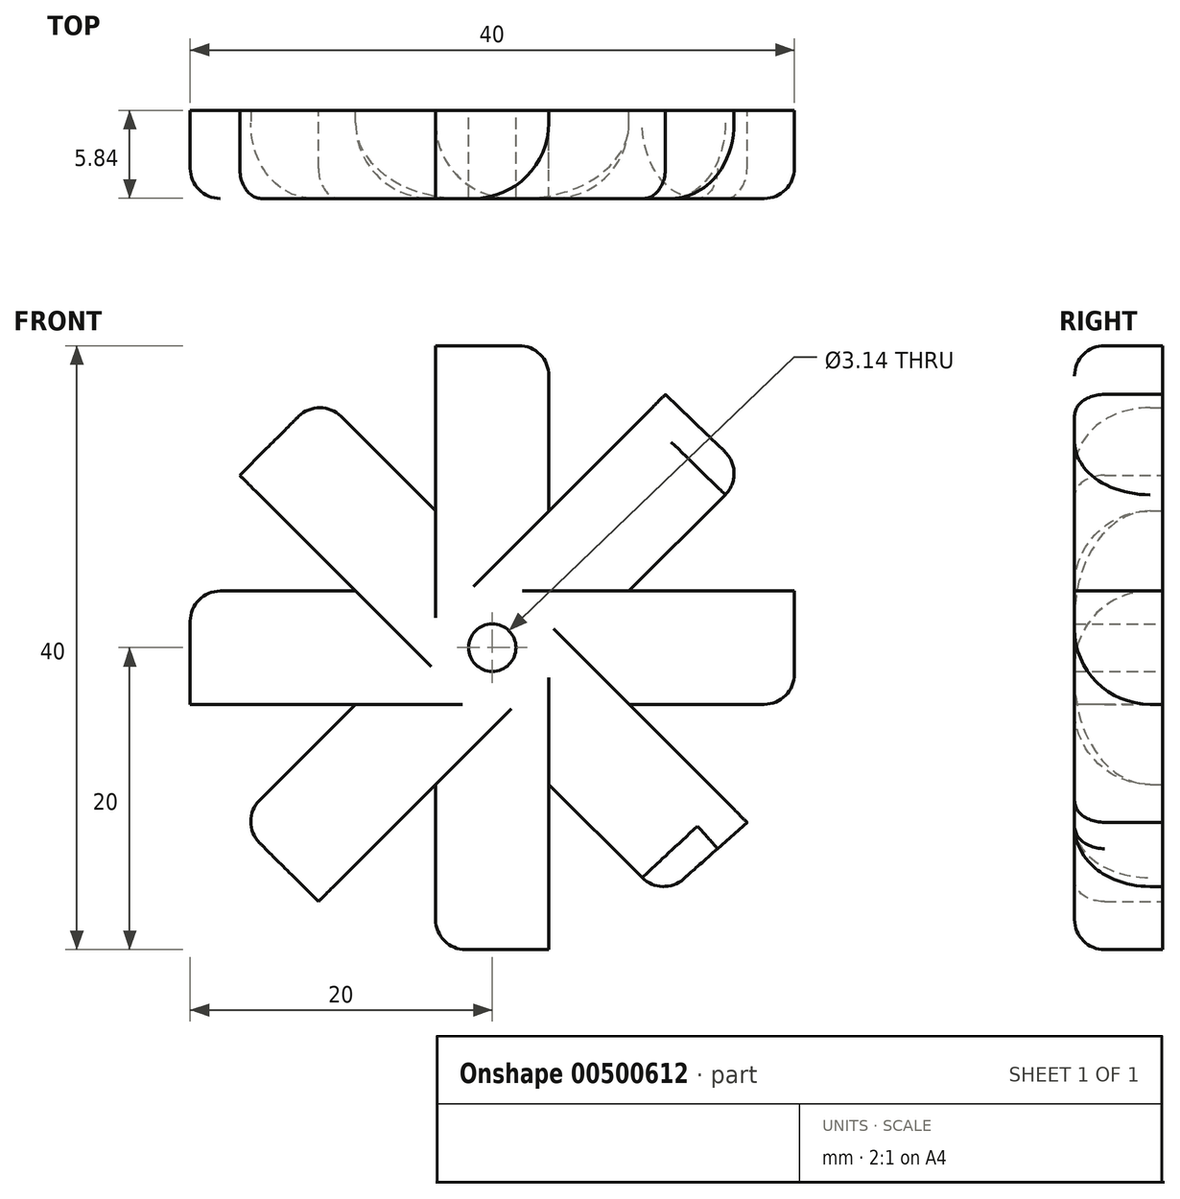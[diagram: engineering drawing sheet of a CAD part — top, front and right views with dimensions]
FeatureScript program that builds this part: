
annotation { "Feature Type Name" : "Feature", "Feature Type Description" : "" }
export const myFeature = defineFeature(function(context is Context, id is Id, definition is map)
    precondition{}
    {
        {
            var Q0;
            Q0=qCreatedBy(makeId("Front.planeOp"),FACE);
            var sketch = newSketch(context, id + "F0", { "sketchPlane" : qUnion([Q0])});
            skCircle(sketch, "E0", {"center": v(0, 0) * mm, "radius": 5 * mm});
            skCircle(sketch, "E1", {"center": v(0, 0) * mm, "radius": 1.57 * mm});
            skLineSegment(sketch, "E2.right", {"start": v(0, 2.75) * mm, "end": v(0, -2.75) * mm});
            skLineSegment(sketch, "E3.bottom", {"start": v(-3.75, 20) * mm, "end": v(3.75, 20) * mm});
            skLineSegment(sketch, "E3.top", {"start": v(-3.75, -20) * mm, "end": v(3.75, -20) * mm});
            skLineSegment(sketch, "E3.left", {"start": v(-3.75, 20) * mm, "end": v(-3.75, -20) * mm});
            skLineSegment(sketch, "E3.right", {"start": v(3.75, 20) * mm, "end": v(3.75, -20) * mm});
            skLineSegment(sketch, "E4", {"start": v(-16.82, -11.51) * mm, "end": v(11.47, 16.77) * mm});
            skLineSegment(sketch, "E5", {"start": v(-16.82, -11.51) * mm, "end": v(-11.51, -16.82) * mm});
            skLineSegment(sketch, "E6", {"start": v(-11.51, -16.82) * mm, "end": v(16.86, 11.56) * mm});
            skLineSegment(sketch, "E7", {"start": v(11.47, 16.77) * mm, "end": v(16.86, 11.56) * mm});
            skPoint(sketch, "E8", {"position": v(3.75, 0) * mm});
            skPoint(sketch, "E9", {"position": v(0, 20) * mm});
            skPoint(sketch, "E10", {"position": v(-14.17, -14.17) * mm});
            skPoint(sketch, "E11", {"position": v(14.17, 14.17) * mm});
            skLineSegment(sketch, "E12.bottom", {"start": v(-20, 3.75) * mm, "end": v(20, 3.75) * mm});
            skLineSegment(sketch, "E12.top", {"start": v(-20, -3.75) * mm, "end": v(20, -3.75) * mm});
            skLineSegment(sketch, "E12.left", {"start": v(-20, 3.75) * mm, "end": v(-20, -3.75) * mm});
            skLineSegment(sketch, "E12.right", {"start": v(20, 3.75) * mm, "end": v(20, -3.75) * mm});
            skPoint(sketch, "E13", {"position": v(-20, 0) * mm});
            skPoint(sketch, "E14", {"position": v(20, 0) * mm});
            skLineSegment(sketch, "E15", {"start": v(-16.72, 11.41) * mm, "end": v(11.26, -16.57) * mm});
            skLineSegment(sketch, "E16", {"start": v(-16.72, 11.41) * mm, "end": v(-11.41, 16.72) * mm});
            skLineSegment(sketch, "E17", {"start": v(-11.41, 16.72) * mm, "end": v(16.87, -11.57) * mm});
            skLineSegment(sketch, "E18", {"start": v(11.26, -16.57) * mm, "end": v(16.87, -11.57) * mm});
            skPoint(sketch, "E19", {"position": v(-14.07, 14.07) * mm});
            skPoint(sketch, "E20", {"position": v(14.07, -14.07) * mm});
            skPoint(sketch, "E21", {"position": v(0, -20) * mm});
            skSolve(sketch);
        }
        {
            var Q0;
            {var subQ1=sQuery(id+"F0.wireOp",EDGE,"E3.bottom");Q0=makeQuery(id+"F0.imprint","IMPRINT",FACE,{"disambiguationData":[TD([[makeQuery(id+"F0.imprint","IMPRINT",EDGE,{"derivedFrom":subQ1}),-1.0]])]});}
            var Q1;
            {var subQ1=sQuery(id+"F0.wireOp",EDGE,"E3.top");Q1=makeQuery(id+"F0.imprint","IMPRINT",FACE,{"disambiguationData":[TD([[makeQuery(id+"F0.imprint","IMPRINT",EDGE,{"derivedFrom":subQ1}),1.0]])]});}
            var Q2;
            {var subQ0=sQuery(id+"F0.wireOp",EDGE,"E16");Q2=makeQuery(id+"F0.imprint","IMPRINT",FACE,{"disambiguationData":[TD([[makeQuery(id+"F0.imprint","IMPRINT",EDGE,{"derivedFrom":subQ0}),-1.0]])]});}
            var Q3;
            {var subQ1=sQuery(id+"F0.wireOp",EDGE,"E5");Q3=makeQuery(id+"F0.imprint","IMPRINT",FACE,{"disambiguationData":[TD([[makeQuery(id+"F0.imprint","IMPRINT",EDGE,{"derivedFrom":subQ1}),1.0]])]});}
            var Q4;
            {var subQ0=sQuery(id+"F0.wireOp",EDGE,"E7");Q4=makeQuery(id+"F0.imprint","IMPRINT",FACE,{"disambiguationData":[TD([[makeQuery(id+"F0.imprint","IMPRINT",EDGE,{"derivedFrom":subQ0}),-1.0]])]});}
            var Q5;
            {var subQ5=sQuery(id+"F0.wireOp",EDGE,"E18");Q5=makeQuery(id+"F0.imprint","IMPRINT",FACE,{"disambiguationData":[TD([[makeQuery(id+"F0.imprint","IMPRINT",EDGE,{"derivedFrom":subQ5}),1.0]])]});}
            var Q6;
            {var subQ0=sQuery(id+"F0.wireOp",EDGE,"E12.left");Q6=makeQuery(id+"F0.imprint","IMPRINT",FACE,{"disambiguationData":[TD([[makeQuery(id+"F0.imprint","IMPRINT",EDGE,{"derivedFrom":subQ0}),1.0]])]});}
            var Q7;
            {var subQ0=sQuery(id+"F0.wireOp",EDGE,"E12.right");Q7=makeQuery(id+"F0.imprint","IMPRINT",FACE,{"disambiguationData":[TD([[makeQuery(id+"F0.imprint","IMPRINT",EDGE,{"derivedFrom":subQ0}),-1.0]])]});}
            var Q8;
            {var subQ3=sQuery(id+"F0.wireOp",EDGE,"E3.right");var subQ5=sQuery(id+"F0.wireOp",EDGE,"E0");var subQ6=makeQuery(id+"F0.imprint","INTERSECT",VERTEX,{"disambiguationData":[OD(0.0)],"derivedFrom":[subQ5,subQ3]});Q8=makeQuery(id+"F0.imprint","IMPRINT",FACE,{"disambiguationData":[TD([[makeQuery(id+"F0.imprint","IMPRINT",EDGE,{"disambiguationData":[TD([[subQ6,1.0]])],"derivedFrom":subQ5}),-1.0]])]});}
            var Q9;
            {var subQ0=sQuery(id+"F0.wireOp",EDGE,"E12.bottom");var subQ1=sQuery(id+"F0.wireOp",EDGE,"E0");var subQ2=makeQuery(id+"F0.imprint","INTERSECT",VERTEX,{"disambiguationData":[OD(0.0)],"derivedFrom":[subQ1,subQ0]});Q9=makeQuery(id+"F0.imprint","IMPRINT",FACE,{"disambiguationData":[TD([[makeQuery(id+"F0.imprint","IMPRINT",EDGE,{"disambiguationData":[TD([[subQ2,-1.0]])],"derivedFrom":subQ1}),-1.0]])]});}
            var Q10;
            {var subQ1=sQuery(id+"F0.wireOp",EDGE,"E0");var subQ5=sQuery(id+"F0.wireOp",EDGE,"E4");var subQ6=makeQuery(id+"F0.imprint","INTERSECT",VERTEX,{"disambiguationData":[OD(0.0)],"derivedFrom":[subQ1,subQ5]});Q10=makeQuery(id+"F0.imprint","IMPRINT",FACE,{"disambiguationData":[TD([[makeQuery(id+"F0.imprint","IMPRINT",EDGE,{"disambiguationData":[TD([[subQ6,-1.0]])],"derivedFrom":subQ1}),-1.0]])]});}
            var Q11;
            {var subQ3=sQuery(id+"F0.wireOp",EDGE,"E3.left");var subQ5=sQuery(id+"F0.wireOp",EDGE,"E0");var subQ6=makeQuery(id+"F0.imprint","INTERSECT",VERTEX,{"disambiguationData":[OD(0.0)],"derivedFrom":[subQ5,subQ3]});Q11=makeQuery(id+"F0.imprint","IMPRINT",FACE,{"disambiguationData":[TD([[makeQuery(id+"F0.imprint","IMPRINT",EDGE,{"disambiguationData":[TD([[subQ6,-1.0]])],"derivedFrom":subQ5}),-1.0]])]});}
            var Q12;
            {var subQ5=sQuery(id+"F0.wireOp",EDGE,"E15");var subQ7=sQuery(id+"F0.wireOp",EDGE,"E0");var subQ9=makeQuery(id+"F0.imprint","INTERSECT",VERTEX,{"disambiguationData":[OD(0.0)],"derivedFrom":[subQ7,subQ5]});Q12=makeQuery(id+"F0.imprint","IMPRINT",FACE,{"disambiguationData":[TD([[makeQuery(id+"F0.imprint","IMPRINT",EDGE,{"disambiguationData":[TD([[subQ9,-1.0]])],"derivedFrom":subQ7}),-1.0]])]});}
            var Q13;
            {var subQ1=sQuery(id+"F0.wireOp",EDGE,"E0");var subQ5=sQuery(id+"F0.wireOp",EDGE,"E6");var subQ6=makeQuery(id+"F0.imprint","INTERSECT",VERTEX,{"disambiguationData":[OD(0.0)],"derivedFrom":[subQ1,subQ5]});Q13=makeQuery(id+"F0.imprint","IMPRINT",FACE,{"disambiguationData":[TD([[makeQuery(id+"F0.imprint","IMPRINT",EDGE,{"disambiguationData":[TD([[subQ6,-1.0]])],"derivedFrom":subQ1}),-1.0]])]});}
            var Q14;
            {var subQ3=sQuery(id+"F0.wireOp",EDGE,"E3.right");var subQ6=sQuery(id+"F0.wireOp",EDGE,"E0");var subQ9=makeQuery(id+"F0.imprint","INTERSECT",VERTEX,{"disambiguationData":[OD(1.0)],"derivedFrom":[subQ6,subQ3]});Q14=makeQuery(id+"F0.imprint","IMPRINT",FACE,{"disambiguationData":[TD([[makeQuery(id+"F0.imprint","IMPRINT",EDGE,{"disambiguationData":[TD([[subQ9,-1.0]])],"derivedFrom":subQ6}),-1.0]])]});}
            var Q15;
            {var subQ1=sQuery(id+"F0.wireOp",EDGE,"E3.bottom");Q15=makeQuery(id+"F0.imprint","IMPRINT",FACE,{"disambiguationData":[TD([[makeQuery(id+"F0.imprint","IMPRINT",EDGE,{"derivedFrom":subQ1}),-1.0]])]});}
            var Q16;
            {var subQ1=sQuery(id+"F0.wireOp",EDGE,"E3.top");Q16=makeQuery(id+"F0.imprint","IMPRINT",FACE,{"disambiguationData":[TD([[makeQuery(id+"F0.imprint","IMPRINT",EDGE,{"derivedFrom":subQ1}),1.0]])]});}
            var Q17;
            {var subQ0=sQuery(id+"F0.wireOp",EDGE,"E16");Q17=makeQuery(id+"F0.imprint","IMPRINT",FACE,{"disambiguationData":[TD([[makeQuery(id+"F0.imprint","IMPRINT",EDGE,{"derivedFrom":subQ0}),-1.0]])]});}
            var Q18;
            {var subQ1=sQuery(id+"F0.wireOp",EDGE,"E5");Q18=makeQuery(id+"F0.imprint","IMPRINT",FACE,{"disambiguationData":[TD([[makeQuery(id+"F0.imprint","IMPRINT",EDGE,{"derivedFrom":subQ1}),1.0]])]});}
            var Q19;
            {var subQ0=sQuery(id+"F0.wireOp",EDGE,"E7");Q19=makeQuery(id+"F0.imprint","IMPRINT",FACE,{"disambiguationData":[TD([[makeQuery(id+"F0.imprint","IMPRINT",EDGE,{"derivedFrom":subQ0}),-1.0]])]});}
            var Q20;
            {var subQ5=sQuery(id+"F0.wireOp",EDGE,"E18");Q20=makeQuery(id+"F0.imprint","IMPRINT",FACE,{"disambiguationData":[TD([[makeQuery(id+"F0.imprint","IMPRINT",EDGE,{"derivedFrom":subQ5}),1.0]])]});}
            var Q21;
            {var subQ0=sQuery(id+"F0.wireOp",EDGE,"E12.left");Q21=makeQuery(id+"F0.imprint","IMPRINT",FACE,{"disambiguationData":[TD([[makeQuery(id+"F0.imprint","IMPRINT",EDGE,{"derivedFrom":subQ0}),1.0]])]});}
            var Q22;
            {var subQ0=sQuery(id+"F0.wireOp",EDGE,"E12.right");Q22=makeQuery(id+"F0.imprint","IMPRINT",FACE,{"disambiguationData":[TD([[makeQuery(id+"F0.imprint","IMPRINT",EDGE,{"derivedFrom":subQ0}),-1.0]])]});}
            var Q23;
            {var subQ3=sQuery(id+"F0.wireOp",EDGE,"E3.right");var subQ5=sQuery(id+"F0.wireOp",EDGE,"E0");var subQ6=makeQuery(id+"F0.imprint","INTERSECT",VERTEX,{"disambiguationData":[OD(0.0)],"derivedFrom":[subQ5,subQ3]});Q23=makeQuery(id+"F0.imprint","IMPRINT",FACE,{"disambiguationData":[TD([[makeQuery(id+"F0.imprint","IMPRINT",EDGE,{"disambiguationData":[TD([[subQ6,1.0]])],"derivedFrom":subQ5}),-1.0]])]});}
            var Q24;
            {var subQ0=sQuery(id+"F0.wireOp",EDGE,"E12.bottom");var subQ1=sQuery(id+"F0.wireOp",EDGE,"E0");var subQ2=makeQuery(id+"F0.imprint","INTERSECT",VERTEX,{"disambiguationData":[OD(0.0)],"derivedFrom":[subQ1,subQ0]});Q24=makeQuery(id+"F0.imprint","IMPRINT",FACE,{"disambiguationData":[TD([[makeQuery(id+"F0.imprint","IMPRINT",EDGE,{"disambiguationData":[TD([[subQ2,-1.0]])],"derivedFrom":subQ1}),-1.0]])]});}
            var Q25;
            {var subQ1=sQuery(id+"F0.wireOp",EDGE,"E0");var subQ5=sQuery(id+"F0.wireOp",EDGE,"E4");var subQ6=makeQuery(id+"F0.imprint","INTERSECT",VERTEX,{"disambiguationData":[OD(0.0)],"derivedFrom":[subQ1,subQ5]});Q25=makeQuery(id+"F0.imprint","IMPRINT",FACE,{"disambiguationData":[TD([[makeQuery(id+"F0.imprint","IMPRINT",EDGE,{"disambiguationData":[TD([[subQ6,-1.0]])],"derivedFrom":subQ1}),-1.0]])]});}
            var Q26;
            {var subQ3=sQuery(id+"F0.wireOp",EDGE,"E3.left");var subQ5=sQuery(id+"F0.wireOp",EDGE,"E0");var subQ6=makeQuery(id+"F0.imprint","INTERSECT",VERTEX,{"disambiguationData":[OD(0.0)],"derivedFrom":[subQ5,subQ3]});Q26=makeQuery(id+"F0.imprint","IMPRINT",FACE,{"disambiguationData":[TD([[makeQuery(id+"F0.imprint","IMPRINT",EDGE,{"disambiguationData":[TD([[subQ6,-1.0]])],"derivedFrom":subQ5}),-1.0]])]});}
            var Q27;
            {var subQ5=sQuery(id+"F0.wireOp",EDGE,"E15");var subQ7=sQuery(id+"F0.wireOp",EDGE,"E0");var subQ9=makeQuery(id+"F0.imprint","INTERSECT",VERTEX,{"disambiguationData":[OD(0.0)],"derivedFrom":[subQ7,subQ5]});Q27=makeQuery(id+"F0.imprint","IMPRINT",FACE,{"disambiguationData":[TD([[makeQuery(id+"F0.imprint","IMPRINT",EDGE,{"disambiguationData":[TD([[subQ9,-1.0]])],"derivedFrom":subQ7}),-1.0]])]});}
            var Q28;
            {var subQ3=sQuery(id+"F0.wireOp",EDGE,"E12.top");var subQ7=sQuery(id+"F0.wireOp",EDGE,"E0");var subQ8=makeQuery(id+"F0.imprint","INTERSECT",VERTEX,{"disambiguationData":[OD(0.0)],"derivedFrom":[subQ7,subQ3]});Q28=makeQuery(id+"F0.imprint","IMPRINT",FACE,{"disambiguationData":[TD([[makeQuery(id+"F0.imprint","IMPRINT",EDGE,{"disambiguationData":[TD([[subQ8,-1.0]])],"derivedFrom":subQ7}),-1.0]])]});}
            var Q29;
            {var subQ1=sQuery(id+"F0.wireOp",EDGE,"E0");var subQ5=sQuery(id+"F0.wireOp",EDGE,"E6");var subQ6=makeQuery(id+"F0.imprint","INTERSECT",VERTEX,{"disambiguationData":[OD(0.0)],"derivedFrom":[subQ1,subQ5]});Q29=makeQuery(id+"F0.imprint","IMPRINT",FACE,{"disambiguationData":[TD([[makeQuery(id+"F0.imprint","IMPRINT",EDGE,{"disambiguationData":[TD([[subQ6,-1.0]])],"derivedFrom":subQ1}),-1.0]])]});}
            var Q30;
            {var subQ3=sQuery(id+"F0.wireOp",EDGE,"E3.right");var subQ6=sQuery(id+"F0.wireOp",EDGE,"E0");var subQ9=makeQuery(id+"F0.imprint","INTERSECT",VERTEX,{"disambiguationData":[OD(1.0)],"derivedFrom":[subQ6,subQ3]});Q30=makeQuery(id+"F0.imprint","IMPRINT",FACE,{"disambiguationData":[TD([[makeQuery(id+"F0.imprint","IMPRINT",EDGE,{"disambiguationData":[TD([[subQ9,-1.0]])],"derivedFrom":subQ6}),-1.0]])]});}
            var Q31;
            {var subQ3=sQuery(id+"F0.wireOp",EDGE,"E3.left");var subQ5=sQuery(id+"F0.wireOp",EDGE,"E0");var subQ6=makeQuery(id+"F0.imprint","INTERSECT",VERTEX,{"disambiguationData":[OD(0.0)],"derivedFrom":[subQ5,subQ3]});Q31=makeQuery(id+"F0.imprint","IMPRINT",FACE,{"disambiguationData":[TD([[makeQuery(id+"F0.imprint","IMPRINT",EDGE,{"disambiguationData":[TD([[subQ6,-1.0]])],"derivedFrom":subQ5}),-1.0]])]});}
            var Q32;
            {var subQ0=sQuery(id+"F0.wireOp",EDGE,"E15");var subQ1=sQuery(id+"F0.wireOp",EDGE,"E0");var subQ2=makeQuery(id+"F0.imprint","INTERSECT",VERTEX,{"disambiguationData":[OD(0.0)],"derivedFrom":[subQ1,subQ0]});Q32=makeQuery(id+"F0.imprint","IMPRINT",FACE,{"disambiguationData":[TD([[makeQuery(id+"F0.imprint","IMPRINT",EDGE,{"disambiguationData":[TD([[subQ2,-1.0]])],"derivedFrom":subQ1}),1.0]])]});}
            var Q33;
            {var subQ1=sQuery(id+"F0.wireOp",EDGE,"E0");var subQ5=sQuery(id+"F0.wireOp",EDGE,"E4");var subQ6=makeQuery(id+"F0.imprint","INTERSECT",VERTEX,{"disambiguationData":[OD(0.0)],"derivedFrom":[subQ1,subQ5]});Q33=makeQuery(id+"F0.imprint","IMPRINT",FACE,{"disambiguationData":[TD([[makeQuery(id+"F0.imprint","IMPRINT",EDGE,{"disambiguationData":[TD([[subQ6,-1.0]])],"derivedFrom":subQ1}),-1.0]])]});}
            var Q34;
            {var subQ0=sQuery(id+"F0.wireOp",EDGE,"E12.bottom");var subQ1=sQuery(id+"F0.wireOp",EDGE,"E0");var subQ2=makeQuery(id+"F0.imprint","INTERSECT",VERTEX,{"disambiguationData":[OD(0.0)],"derivedFrom":[subQ1,subQ0]});Q34=makeQuery(id+"F0.imprint","IMPRINT",FACE,{"disambiguationData":[TD([[makeQuery(id+"F0.imprint","IMPRINT",EDGE,{"disambiguationData":[TD([[subQ2,-1.0]])],"derivedFrom":subQ1}),-1.0]])]});}
            var Q35;
            {var subQ0=sQuery(id+"F0.wireOp",EDGE,"E17");var subQ1=sQuery(id+"F0.wireOp",EDGE,"E0");var subQ2=makeQuery(id+"F0.imprint","INTERSECT",VERTEX,{"disambiguationData":[OD(1.0)],"derivedFrom":[subQ1,subQ0]});Q35=makeQuery(id+"F0.imprint","IMPRINT",FACE,{"disambiguationData":[TD([[makeQuery(id+"F0.imprint","IMPRINT",EDGE,{"disambiguationData":[TD([[subQ2,-1.0]])],"derivedFrom":subQ1}),1.0]])]});}
            var Q36;
            {var subQ0=sQuery(id+"F0.wireOp",EDGE,"E17");var subQ1=sQuery(id+"F0.wireOp",EDGE,"E0");var subQ2=makeQuery(id+"F0.imprint","INTERSECT",VERTEX,{"disambiguationData":[OD(0.0)],"derivedFrom":[subQ1,subQ0]});Q36=makeQuery(id+"F0.imprint","IMPRINT",FACE,{"disambiguationData":[TD([[makeQuery(id+"F0.imprint","IMPRINT",EDGE,{"disambiguationData":[TD([[subQ2,1.0]])],"derivedFrom":subQ1}),1.0]])]});}
            var Q37;
            {var subQ0=sQuery(id+"F0.wireOp",EDGE,"E4");var subQ1=sQuery(id+"F0.wireOp",EDGE,"E0");var subQ2=makeQuery(id+"F0.imprint","INTERSECT",VERTEX,{"disambiguationData":[OD(1.0)],"derivedFrom":[subQ1,subQ0]});Q37=makeQuery(id+"F0.imprint","IMPRINT",FACE,{"disambiguationData":[TD([[makeQuery(id+"F0.imprint","IMPRINT",EDGE,{"disambiguationData":[TD([[subQ2,-1.0]])],"derivedFrom":subQ1}),1.0]])]});}
            var Q38;
            {var subQ1=sQuery(id+"F0.wireOp",EDGE,"E0");var subQ5=sQuery(id+"F0.wireOp",EDGE,"E6");var subQ6=makeQuery(id+"F0.imprint","INTERSECT",VERTEX,{"disambiguationData":[OD(0.0)],"derivedFrom":[subQ1,subQ5]});Q38=makeQuery(id+"F0.imprint","IMPRINT",FACE,{"disambiguationData":[TD([[makeQuery(id+"F0.imprint","IMPRINT",EDGE,{"disambiguationData":[TD([[subQ6,-1.0]])],"derivedFrom":subQ1}),-1.0]])]});}
            var Q39;
            {var subQ0=sQuery(id+"F0.wireOp",EDGE,"E15");var subQ1=sQuery(id+"F0.wireOp",EDGE,"E0");var subQ2=makeQuery(id+"F0.imprint","INTERSECT",VERTEX,{"disambiguationData":[OD(1.0)],"derivedFrom":[subQ1,subQ0]});Q39=makeQuery(id+"F0.imprint","IMPRINT",FACE,{"disambiguationData":[TD([[makeQuery(id+"F0.imprint","IMPRINT",EDGE,{"disambiguationData":[TD([[subQ2,-1.0]])],"derivedFrom":subQ1}),-1.0]])]});}
            var Q40;
            {var subQ0=sQuery(id+"F0.wireOp",EDGE,"E12.bottom");var subQ1=sQuery(id+"F0.wireOp",EDGE,"E0");var subQ2=makeQuery(id+"F0.imprint","INTERSECT",VERTEX,{"disambiguationData":[OD(1.0)],"derivedFrom":[subQ1,subQ0]});Q40=makeQuery(id+"F0.imprint","IMPRINT",FACE,{"disambiguationData":[TD([[makeQuery(id+"F0.imprint","IMPRINT",EDGE,{"disambiguationData":[TD([[subQ2,-1.0]])],"derivedFrom":subQ1}),-1.0]])]});}
            var Q41;
            {var subQ10=sQuery(id+"F0.wireOp",EDGE,"E2.right");var subQ11=sQuery(id+"F0.wireOp",EDGE,"E1");var subQ12=makeQuery(id+"F0.imprint","INTERSECT",VERTEX,{"disambiguationData":[OD(0.0)],"derivedFrom":[subQ11,subQ10]});Q41=makeQuery(id+"F0.imprint","IMPRINT",FACE,{"disambiguationData":[TD([[makeQuery(id+"F0.imprint","IMPRINT",EDGE,{"disambiguationData":[TD([[subQ12,1.0]])],"derivedFrom":subQ11}),-1.0]])]});}
            var Q42;
            {var subQ0=sQuery(id+"F0.wireOp",EDGE,"E3.left");var subQ1=sQuery(id+"F0.wireOp",EDGE,"E0");var subQ2=makeQuery(id+"F0.imprint","INTERSECT",VERTEX,{"disambiguationData":[OD(1.0)],"derivedFrom":[subQ1,subQ0]});Q42=makeQuery(id+"F0.imprint","IMPRINT",FACE,{"disambiguationData":[TD([[makeQuery(id+"F0.imprint","IMPRINT",EDGE,{"disambiguationData":[TD([[subQ2,-1.0]])],"derivedFrom":subQ1}),1.0]])]});}
            var Q43;
            {var subQ3=sQuery(id+"F0.wireOp",EDGE,"E3.right");var subQ5=sQuery(id+"F0.wireOp",EDGE,"E0");var subQ6=makeQuery(id+"F0.imprint","INTERSECT",VERTEX,{"disambiguationData":[OD(0.0)],"derivedFrom":[subQ5,subQ3]});Q43=makeQuery(id+"F0.imprint","IMPRINT",FACE,{"disambiguationData":[TD([[makeQuery(id+"F0.imprint","IMPRINT",EDGE,{"disambiguationData":[TD([[subQ6,1.0]])],"derivedFrom":subQ5}),-1.0]])]});}
            var Q44;
            {var subQ10=sQuery(id+"F0.wireOp",EDGE,"E2.right");var subQ11=sQuery(id+"F0.wireOp",EDGE,"E1");var subQ12=makeQuery(id+"F0.imprint","INTERSECT",VERTEX,{"disambiguationData":[OD(0.0)],"derivedFrom":[subQ11,subQ10]});Q44=makeQuery(id+"F0.imprint","IMPRINT",FACE,{"disambiguationData":[TD([[makeQuery(id+"F0.imprint","IMPRINT",EDGE,{"disambiguationData":[TD([[subQ12,1.0]])],"derivedFrom":subQ11}),-1.0]])]});}
            var Q45;
            {var subQ0=sQuery(id+"F0.wireOp",EDGE,"E12.top");var subQ1=sQuery(id+"F0.wireOp",EDGE,"E0");var subQ2=makeQuery(id+"F0.imprint","INTERSECT",VERTEX,{"disambiguationData":[OD(1.0)],"derivedFrom":[subQ1,subQ0]});Q45=makeQuery(id+"F0.imprint","IMPRINT",FACE,{"disambiguationData":[TD([[makeQuery(id+"F0.imprint","IMPRINT",EDGE,{"disambiguationData":[TD([[subQ2,-1.0]])],"derivedFrom":subQ1}),1.0]])]});}
            var Q46;
            {var subQ0=sQuery(id+"F0.wireOp",EDGE,"E3.right");var subQ1=sQuery(id+"F0.wireOp",EDGE,"E0");var subQ2=makeQuery(id+"F0.imprint","INTERSECT",VERTEX,{"disambiguationData":[OD(0.0)],"derivedFrom":[subQ1,subQ0]});Q46=makeQuery(id+"F0.imprint","IMPRINT",FACE,{"disambiguationData":[TD([[makeQuery(id+"F0.imprint","IMPRINT",EDGE,{"disambiguationData":[TD([[subQ2,-1.0]])],"derivedFrom":subQ1}),-1.0]])]});}
            var Q47;
            {var subQ0=sQuery(id+"F0.wireOp",EDGE,"E3.right");var subQ1=sQuery(id+"F0.wireOp",EDGE,"E0");var subQ2=makeQuery(id+"F0.imprint","INTERSECT",VERTEX,{"disambiguationData":[OD(1.0)],"derivedFrom":[subQ1,subQ0]});Q47=makeQuery(id+"F0.imprint","IMPRINT",FACE,{"disambiguationData":[TD([[makeQuery(id+"F0.imprint","IMPRINT",EDGE,{"disambiguationData":[TD([[subQ2,-1.0]])],"derivedFrom":subQ1}),1.0]])]});}
            var Q48;
            {var subQ0=sQuery(id+"F0.wireOp",EDGE,"E15");var subQ1=sQuery(id+"F0.wireOp",EDGE,"E0");var subQ2=makeQuery(id+"F0.imprint","INTERSECT",VERTEX,{"disambiguationData":[OD(1.0)],"derivedFrom":[subQ1,subQ0]});Q48=makeQuery(id+"F0.imprint","IMPRINT",FACE,{"disambiguationData":[TD([[makeQuery(id+"F0.imprint","IMPRINT",EDGE,{"disambiguationData":[TD([[subQ2,-1.0]])],"derivedFrom":subQ1}),1.0]])]});}
            var Q49;
            {var subQ0=sQuery(id+"F0.wireOp",EDGE,"E3.right");var subQ1=sQuery(id+"F0.wireOp",EDGE,"E0");var subQ2=makeQuery(id+"F0.imprint","INTERSECT",VERTEX,{"disambiguationData":[OD(1.0)],"derivedFrom":[subQ1,subQ0]});Q49=makeQuery(id+"F0.imprint","IMPRINT",FACE,{"disambiguationData":[TD([[makeQuery(id+"F0.imprint","IMPRINT",EDGE,{"disambiguationData":[TD([[subQ2,-1.0]])],"derivedFrom":subQ1}),1.0]])]});}
            var Q50;
            {var subQ0=sQuery(id+"F0.wireOp",EDGE,"E12.bottom");var subQ1=sQuery(id+"F0.wireOp",EDGE,"E0");var subQ2=makeQuery(id+"F0.imprint","INTERSECT",VERTEX,{"disambiguationData":[OD(1.0)],"derivedFrom":[subQ1,subQ0]});Q50=makeQuery(id+"F0.imprint","IMPRINT",FACE,{"disambiguationData":[TD([[makeQuery(id+"F0.imprint","IMPRINT",EDGE,{"disambiguationData":[TD([[subQ2,-1.0]])],"derivedFrom":subQ1}),1.0]])]});}
            var Q51;
            {var subQ0=sQuery(id+"F0.wireOp",EDGE,"E3.left");var subQ1=sQuery(id+"F0.wireOp",EDGE,"E0");var subQ2=makeQuery(id+"F0.imprint","INTERSECT",VERTEX,{"disambiguationData":[OD(0.0)],"derivedFrom":[subQ1,subQ0]});Q51=makeQuery(id+"F0.imprint","IMPRINT",FACE,{"disambiguationData":[TD([[makeQuery(id+"F0.imprint","IMPRINT",EDGE,{"disambiguationData":[TD([[subQ2,-1.0]])],"derivedFrom":subQ1}),1.0]])]});}
            var Q52;
            {var subQ0=sQuery(id+"F0.wireOp",EDGE,"E4");var subQ1=sQuery(id+"F0.wireOp",EDGE,"E0");var subQ2=makeQuery(id+"F0.imprint","INTERSECT",VERTEX,{"disambiguationData":[OD(0.0)],"derivedFrom":[subQ1,subQ0]});Q52=makeQuery(id+"F0.imprint","IMPRINT",FACE,{"disambiguationData":[TD([[makeQuery(id+"F0.imprint","IMPRINT",EDGE,{"disambiguationData":[TD([[subQ2,-1.0]])],"derivedFrom":subQ1}),1.0]])]});}
            var Q53;
            {var subQ0=sQuery(id+"F0.wireOp",EDGE,"E12.top");var subQ1=sQuery(id+"F0.wireOp",EDGE,"E0");var subQ2=makeQuery(id+"F0.imprint","INTERSECT",VERTEX,{"disambiguationData":[OD(0.0)],"derivedFrom":[subQ1,subQ0]});Q53=makeQuery(id+"F0.imprint","IMPRINT",FACE,{"disambiguationData":[TD([[makeQuery(id+"F0.imprint","IMPRINT",EDGE,{"disambiguationData":[TD([[subQ2,-1.0]])],"derivedFrom":subQ1}),1.0]])]});}
            var Q54;
            {var subQ0=sQuery(id+"F0.wireOp",EDGE,"E6");var subQ1=sQuery(id+"F0.wireOp",EDGE,"E0");var subQ2=makeQuery(id+"F0.imprint","INTERSECT",VERTEX,{"disambiguationData":[OD(0.0)],"derivedFrom":[subQ1,subQ0]});Q54=makeQuery(id+"F0.imprint","IMPRINT",FACE,{"disambiguationData":[TD([[makeQuery(id+"F0.imprint","IMPRINT",EDGE,{"disambiguationData":[TD([[subQ2,-1.0]])],"derivedFrom":subQ1}),1.0]])]});}
            var Q55;
            {var subQ0=sQuery(id+"F0.wireOp",EDGE,"E3.right");var subQ1=sQuery(id+"F0.wireOp",EDGE,"E0");var subQ2=makeQuery(id+"F0.imprint","INTERSECT",VERTEX,{"disambiguationData":[OD(0.0)],"derivedFrom":[subQ1,subQ0]});Q55=makeQuery(id+"F0.imprint","IMPRINT",FACE,{"disambiguationData":[TD([[makeQuery(id+"F0.imprint","IMPRINT",EDGE,{"disambiguationData":[TD([[subQ2,-1.0]])],"derivedFrom":subQ1}),1.0]])]});}
            var Q56;
            {var subQ0=sQuery(id+"F0.wireOp",EDGE,"E12.bottom");var subQ1=sQuery(id+"F0.wireOp",EDGE,"E0");var subQ2=makeQuery(id+"F0.imprint","INTERSECT",VERTEX,{"disambiguationData":[OD(0.0)],"derivedFrom":[subQ1,subQ0]});Q56=makeQuery(id+"F0.imprint","IMPRINT",FACE,{"disambiguationData":[TD([[makeQuery(id+"F0.imprint","IMPRINT",EDGE,{"disambiguationData":[TD([[subQ2,-1.0]])],"derivedFrom":subQ1}),1.0]])]});}
            var Q57;
            {var subQ0=sQuery(id+"F0.wireOp",EDGE,"E3.right");var subQ1=sQuery(id+"F0.wireOp",EDGE,"E0");var subQ2=makeQuery(id+"F0.imprint","INTERSECT",VERTEX,{"disambiguationData":[OD(0.0)],"derivedFrom":[subQ1,subQ0]});Q57=makeQuery(id+"F0.imprint","IMPRINT",FACE,{"disambiguationData":[TD([[makeQuery(id+"F0.imprint","IMPRINT",EDGE,{"disambiguationData":[TD([[subQ2,1.0]])],"derivedFrom":subQ1}),1.0]])]});}
            var Q58;
            {var subQ0=sQuery(id+"F0.wireOp",EDGE,"E4");var subQ1=sQuery(id+"F0.wireOp",EDGE,"E0");var subQ2=makeQuery(id+"F0.imprint","INTERSECT",VERTEX,{"disambiguationData":[OD(1.0)],"derivedFrom":[subQ1,subQ0]});Q58=makeQuery(id+"F0.imprint","IMPRINT",FACE,{"disambiguationData":[TD([[makeQuery(id+"F0.imprint","IMPRINT",EDGE,{"disambiguationData":[TD([[subQ2,-1.0]])],"derivedFrom":subQ1}),-1.0]])]});}
            var Q59;
            {var subQ0=sQuery(id+"F0.wireOp",EDGE,"E17");var subQ1=sQuery(id+"F0.wireOp",EDGE,"E0");var subQ2=makeQuery(id+"F0.imprint","INTERSECT",VERTEX,{"disambiguationData":[OD(1.0)],"derivedFrom":[subQ1,subQ0]});Q59=makeQuery(id+"F0.imprint","IMPRINT",FACE,{"disambiguationData":[TD([[makeQuery(id+"F0.imprint","IMPRINT",EDGE,{"disambiguationData":[TD([[subQ2,-1.0]])],"derivedFrom":subQ1}),-1.0]])]});}
            var Q60;
            {var subQ0=sQuery(id+"F0.wireOp",EDGE,"E17");var subQ1=sQuery(id+"F0.wireOp",EDGE,"E0");var subQ2=makeQuery(id+"F0.imprint","INTERSECT",VERTEX,{"disambiguationData":[OD(0.0)],"derivedFrom":[subQ1,subQ0]});Q60=makeQuery(id+"F0.imprint","IMPRINT",FACE,{"disambiguationData":[TD([[makeQuery(id+"F0.imprint","IMPRINT",EDGE,{"disambiguationData":[TD([[subQ2,1.0]])],"derivedFrom":subQ1}),-1.0]])]});}
            var Q61;
            {var subQ0=sQuery(id+"F0.wireOp",EDGE,"E12.top");var subQ1=sQuery(id+"F0.wireOp",EDGE,"E0");var subQ2=makeQuery(id+"F0.imprint","INTERSECT",VERTEX,{"disambiguationData":[OD(1.0)],"derivedFrom":[subQ1,subQ0]});Q61=makeQuery(id+"F0.imprint","IMPRINT",FACE,{"disambiguationData":[TD([[makeQuery(id+"F0.imprint","IMPRINT",EDGE,{"disambiguationData":[TD([[subQ2,-1.0]])],"derivedFrom":subQ1}),-1.0]])]});}
            var Q62;
            {var subQ0=sQuery(id+"F0.wireOp",EDGE,"E3.left");var subQ1=sQuery(id+"F0.wireOp",EDGE,"E0");var subQ2=makeQuery(id+"F0.imprint","INTERSECT",VERTEX,{"disambiguationData":[OD(1.0)],"derivedFrom":[subQ1,subQ0]});Q62=makeQuery(id+"F0.imprint","IMPRINT",FACE,{"disambiguationData":[TD([[makeQuery(id+"F0.imprint","IMPRINT",EDGE,{"disambiguationData":[TD([[subQ2,-1.0]])],"derivedFrom":subQ1}),-1.0]])]});}
            extrude(context, id + "F1", {"entities" : qUnion([Q0, Q1, Q2, Q3, Q4, Q5, Q6, Q7, Q8, Q9, Q10, Q11, Q12, Q13, Q14, Q15, Q16, Q17, Q18, Q19, Q20, Q21, Q22, Q23, Q24, Q25, Q26, Q27, Q28, Q29, Q30, Q31, Q32, Q33, Q34, Q35, Q36, Q37, Q38, Q39, Q40, Q41, Q42, Q43, Q44, Q45, Q46, Q47, Q48, Q49, Q50, Q51, Q52, Q53, Q54, Q55, Q56, Q57, Q58, Q59, Q60, Q61, Q62]), "depth" : 5.84 * mm});
        }
        {
            var Q0;
            {var subQ0=sQuery(id+"F0.wireOp",EDGE,"E17");Q0=makeQuery(id+"F1.opExtrude","CAP_EDGE",EDGE,{"disambiguationData":[OSD([subQ0]),TDD([makeQuery(id+"F0.imprint","IMPRINT",EDGE,{"disambiguationData":[TD([[makeQuery(id+"F0.imprint","INTERSECT",VERTEX,{"derivedFrom":[sQuery(id+"F0.wireOp",EDGE,"E16"),subQ0]}),-1.0]])],"derivedFrom":subQ0})])],"isStart":false});}
            var Q1;
            {var subQ0=sQuery(id+"F0.wireOp",EDGE,"E3.right");Q1=makeQuery(id+"F1.opExtrude","CAP_EDGE",EDGE,{"disambiguationData":[OSD([subQ0]),TDD([makeQuery(id+"F0.imprint","IMPRINT",EDGE,{"disambiguationData":[TD([[makeQuery(id+"F0.imprint","INTERSECT",VERTEX,{"derivedFrom":[sQuery(id+"F0.wireOp",EDGE,"E3.bottom"),subQ0]}),-1.0]])],"derivedFrom":subQ0})])],"isStart":false});}
            var Q2;
            {var subQ0=sQuery(id+"F0.wireOp",EDGE,"E6");Q2=makeQuery(id+"F1.opExtrude","CAP_EDGE",EDGE,{"disambiguationData":[OSD([subQ0]),TDD([makeQuery(id+"F0.imprint","IMPRINT",EDGE,{"disambiguationData":[TD([[makeQuery(id+"F0.imprint","INTERSECT",VERTEX,{"derivedFrom":[subQ0,sQuery(id+"F0.wireOp",EDGE,"E7")]}),1.0]])],"derivedFrom":subQ0})])],"isStart":false});}
            var Q3;
            {var subQ0=sQuery(id+"F0.wireOp",EDGE,"E12.top");Q3=makeQuery(id+"F1.opExtrude","CAP_EDGE",EDGE,{"disambiguationData":[OSD([subQ0]),TDD([makeQuery(id+"F0.imprint","IMPRINT",EDGE,{"disambiguationData":[TD([[makeQuery(id+"F0.imprint","INTERSECT",VERTEX,{"derivedFrom":[subQ0,sQuery(id+"F0.wireOp",EDGE,"E12.right")]}),1.0]])],"derivedFrom":subQ0})])],"isStart":false});}
            var Q4;
            {var subQ0=sQuery(id+"F0.wireOp",EDGE,"E15");Q4=makeQuery(id+"F1.opExtrude","CAP_EDGE",EDGE,{"disambiguationData":[OSD([subQ0]),TDD([makeQuery(id+"F0.imprint","IMPRINT",EDGE,{"disambiguationData":[TD([[makeQuery(id+"F0.imprint","INTERSECT",VERTEX,{"derivedFrom":[subQ0,sQuery(id+"F0.wireOp",EDGE,"E18")]}),1.0]])],"derivedFrom":subQ0})])],"isStart":false});}
            var Q5;
            {var subQ0=sQuery(id+"F0.wireOp",EDGE,"E3.left");Q5=makeQuery(id+"F1.opExtrude","CAP_EDGE",EDGE,{"disambiguationData":[OSD([subQ0]),TDD([makeQuery(id+"F0.imprint","IMPRINT",EDGE,{"disambiguationData":[TD([[makeQuery(id+"F0.imprint","INTERSECT",VERTEX,{"derivedFrom":[sQuery(id+"F0.wireOp",EDGE,"E3.top"),subQ0]}),1.0]])],"derivedFrom":subQ0})])],"isStart":false});}
            var Q6;
            {var subQ0=sQuery(id+"F0.wireOp",EDGE,"E4");Q6=makeQuery(id+"F1.opExtrude","CAP_EDGE",EDGE,{"disambiguationData":[OSD([subQ0]),TDD([makeQuery(id+"F0.imprint","IMPRINT",EDGE,{"disambiguationData":[TD([[makeQuery(id+"F0.imprint","INTERSECT",VERTEX,{"derivedFrom":[subQ0,sQuery(id+"F0.wireOp",EDGE,"E5")]}),-1.0]])],"derivedFrom":subQ0})])],"isStart":false});}
            var Q7;
            {var subQ0=sQuery(id+"F0.wireOp",EDGE,"E12.bottom");Q7=makeQuery(id+"F1.opExtrude","CAP_EDGE",EDGE,{"disambiguationData":[OSD([subQ0]),TDD([makeQuery(id+"F0.imprint","IMPRINT",EDGE,{"disambiguationData":[TD([[makeQuery(id+"F0.imprint","INTERSECT",VERTEX,{"derivedFrom":[subQ0,sQuery(id+"F0.wireOp",EDGE,"E12.left")]}),-1.0]])],"derivedFrom":subQ0})])],"isStart":false});}
            fillet(context, id + "F2", {"entities" : qUnion([Q0, Q1, Q2, Q3, Q4, Q5, Q6, Q7]), "radius" : 5 * mm, "tangentPropagation" : true, "allowEdgeOverflow" : false});
        }
        {
            var Q0;
            Q0=makeQuery(id+"F1.opExtrude","CAP_EDGE",EDGE,{"disambiguationData":[OSD([sQuery(id+"F0.wireOp",EDGE,"E3.bottom")])],"isStart":false});
            var Q1;
            {var subQ0=sQuery(id+"F0.wireOp",EDGE,"E3.bottom");var subQ1=sQuery(id+"F0.wireOp",EDGE,"E3.right");Q1=makeQuery(id+"F2.opFillet","BLEND_EDGE",EDGE,{"blendedFrom":[makeQuery(id+"F1.opExtrude","CAP_EDGE",EDGE,{"disambiguationData":[OSD([subQ1]),TDD([makeQuery(id+"F0.imprint","IMPRINT",EDGE,{"disambiguationData":[TD([[makeQuery(id+"F0.imprint","INTERSECT",VERTEX,{"derivedFrom":[subQ0,subQ1]}),-1.0]])],"derivedFrom":subQ1})])],"isStart":false}),makeQuery(id+"F1.opExtrude","SWEPT_FACE",FACE,{"disambiguationData":[OSD([subQ0])]})],"blendedInto":[makeQuery(id+"F1.opExtrude","SWEPT_FACE",FACE,{"disambiguationData":[OSD([subQ0])]})]});}
            var Q2;
            Q2=makeQuery(id+"F1.opExtrude","CAP_EDGE",EDGE,{"disambiguationData":[OSD([sQuery(id+"F0.wireOp",EDGE,"E7")])],"isStart":false});
            var Q3;
            {var subQ0=sQuery(id+"F0.wireOp",EDGE,"E7");var subQ1=sQuery(id+"F0.wireOp",EDGE,"E6");Q3=makeQuery(id+"F2.opFillet","BLEND_EDGE",EDGE,{"blendedFrom":[makeQuery(id+"F1.opExtrude","CAP_EDGE",EDGE,{"disambiguationData":[OSD([subQ1]),TDD([makeQuery(id+"F0.imprint","IMPRINT",EDGE,{"disambiguationData":[TD([[makeQuery(id+"F0.imprint","INTERSECT",VERTEX,{"derivedFrom":[subQ1,subQ0]}),1.0]])],"derivedFrom":subQ1})])],"isStart":false}),makeQuery(id+"F1.opExtrude","SWEPT_FACE",FACE,{"disambiguationData":[OSD([subQ0])]})],"blendedInto":[makeQuery(id+"F1.opExtrude","SWEPT_FACE",FACE,{"disambiguationData":[OSD([subQ0])]})]});}
            var Q4;
            Q4=makeQuery(id+"F1.opExtrude","CAP_EDGE",EDGE,{"disambiguationData":[OSD([sQuery(id+"F0.wireOp",EDGE,"E12.right")])],"isStart":false});
            var Q5;
            {var subQ0=sQuery(id+"F0.wireOp",EDGE,"E12.right");var subQ1=sQuery(id+"F0.wireOp",EDGE,"E12.top");Q5=makeQuery(id+"F2.opFillet","BLEND_EDGE",EDGE,{"blendedFrom":[makeQuery(id+"F1.opExtrude","CAP_EDGE",EDGE,{"disambiguationData":[OSD([subQ1]),TDD([makeQuery(id+"F0.imprint","IMPRINT",EDGE,{"disambiguationData":[TD([[makeQuery(id+"F0.imprint","INTERSECT",VERTEX,{"derivedFrom":[subQ1,subQ0]}),1.0]])],"derivedFrom":subQ1})])],"isStart":false}),makeQuery(id+"F1.opExtrude","SWEPT_FACE",FACE,{"disambiguationData":[OSD([subQ0])]})],"blendedInto":[makeQuery(id+"F1.opExtrude","SWEPT_FACE",FACE,{"disambiguationData":[OSD([subQ0])]})]});}
            var Q6;
            {var subQ0=sQuery(id+"F0.wireOp",EDGE,"E16");var subQ1=sQuery(id+"F0.wireOp",EDGE,"E17");Q6=makeQuery(id+"F2.opFillet","BLEND_EDGE",EDGE,{"blendedFrom":[makeQuery(id+"F1.opExtrude","CAP_EDGE",EDGE,{"disambiguationData":[OSD([subQ1]),TDD([makeQuery(id+"F0.imprint","IMPRINT",EDGE,{"disambiguationData":[TD([[makeQuery(id+"F0.imprint","INTERSECT",VERTEX,{"derivedFrom":[subQ0,subQ1]}),-1.0]])],"derivedFrom":subQ1})])],"isStart":false}),makeQuery(id+"F1.opExtrude","SWEPT_FACE",FACE,{"disambiguationData":[OSD([subQ0])]})],"blendedInto":[makeQuery(id+"F1.opExtrude","SWEPT_FACE",FACE,{"disambiguationData":[OSD([subQ0])]})]});}
            var Q7;
            Q7=makeQuery(id+"F1.opExtrude","CAP_EDGE",EDGE,{"disambiguationData":[OSD([sQuery(id+"F0.wireOp",EDGE,"E16")])],"isStart":false});
            var Q8;
            Q8=makeQuery(id+"F1.opExtrude","CAP_EDGE",EDGE,{"disambiguationData":[OSD([sQuery(id+"F0.wireOp",EDGE,"E12.left")])],"isStart":false});
            var Q9;
            {var subQ0=sQuery(id+"F0.wireOp",EDGE,"E12.left");var subQ1=sQuery(id+"F0.wireOp",EDGE,"E12.bottom");Q9=makeQuery(id+"F2.opFillet","BLEND_EDGE",EDGE,{"blendedFrom":[makeQuery(id+"F1.opExtrude","CAP_EDGE",EDGE,{"disambiguationData":[OSD([subQ1]),TDD([makeQuery(id+"F0.imprint","IMPRINT",EDGE,{"disambiguationData":[TD([[makeQuery(id+"F0.imprint","INTERSECT",VERTEX,{"derivedFrom":[subQ1,subQ0]}),-1.0]])],"derivedFrom":subQ1})])],"isStart":false}),makeQuery(id+"F1.opExtrude","SWEPT_FACE",FACE,{"disambiguationData":[OSD([subQ0])]})],"blendedInto":[makeQuery(id+"F1.opExtrude","SWEPT_FACE",FACE,{"disambiguationData":[OSD([subQ0])]})]});}
            var Q10;
            Q10=makeQuery(id+"F1.opExtrude","CAP_EDGE",EDGE,{"disambiguationData":[OSD([sQuery(id+"F0.wireOp",EDGE,"E5")])],"isStart":false});
            var Q11;
            {var subQ0=sQuery(id+"F0.wireOp",EDGE,"E5");var subQ1=sQuery(id+"F0.wireOp",EDGE,"E4");Q11=makeQuery(id+"F2.opFillet","BLEND_EDGE",EDGE,{"blendedFrom":[makeQuery(id+"F1.opExtrude","CAP_EDGE",EDGE,{"disambiguationData":[OSD([subQ1]),TDD([makeQuery(id+"F0.imprint","IMPRINT",EDGE,{"disambiguationData":[TD([[makeQuery(id+"F0.imprint","INTERSECT",VERTEX,{"derivedFrom":[subQ1,subQ0]}),-1.0]])],"derivedFrom":subQ1})])],"isStart":false}),makeQuery(id+"F1.opExtrude","SWEPT_FACE",FACE,{"disambiguationData":[OSD([subQ0])]})],"blendedInto":[makeQuery(id+"F1.opExtrude","SWEPT_FACE",FACE,{"disambiguationData":[OSD([subQ0])]})]});}
            var Q12;
            {var subQ0=sQuery(id+"F0.wireOp",EDGE,"E3.top");var subQ1=sQuery(id+"F0.wireOp",EDGE,"E3.left");Q12=makeQuery(id+"F2.opFillet","BLEND_EDGE",EDGE,{"blendedFrom":[makeQuery(id+"F1.opExtrude","CAP_EDGE",EDGE,{"disambiguationData":[OSD([subQ1]),TDD([makeQuery(id+"F0.imprint","IMPRINT",EDGE,{"disambiguationData":[TD([[makeQuery(id+"F0.imprint","INTERSECT",VERTEX,{"derivedFrom":[subQ0,subQ1]}),1.0]])],"derivedFrom":subQ1})])],"isStart":false}),makeQuery(id+"F1.opExtrude","SWEPT_FACE",FACE,{"disambiguationData":[OSD([subQ0])]})],"blendedInto":[makeQuery(id+"F1.opExtrude","SWEPT_FACE",FACE,{"disambiguationData":[OSD([subQ0])]})]});}
            var Q13;
            Q13=makeQuery(id+"F1.opExtrude","CAP_EDGE",EDGE,{"disambiguationData":[OSD([sQuery(id+"F0.wireOp",EDGE,"E3.top")])],"isStart":false});
            var Q14;
            Q14=makeQuery(id+"F1.opExtrude","CAP_EDGE",EDGE,{"disambiguationData":[OSD([sQuery(id+"F0.wireOp",EDGE,"E18")])],"isStart":false});
            var Q15;
            {var subQ0=sQuery(id+"F0.wireOp",EDGE,"E18");var subQ1=sQuery(id+"F0.wireOp",EDGE,"E15");Q15=makeQuery(id+"F2.opFillet","BLEND_EDGE",EDGE,{"blendedFrom":[makeQuery(id+"F1.opExtrude","CAP_EDGE",EDGE,{"disambiguationData":[OSD([subQ1]),TDD([makeQuery(id+"F0.imprint","IMPRINT",EDGE,{"disambiguationData":[TD([[makeQuery(id+"F0.imprint","INTERSECT",VERTEX,{"derivedFrom":[subQ1,subQ0]}),1.0]])],"derivedFrom":subQ1})])],"isStart":false}),makeQuery(id+"F1.opExtrude","SWEPT_FACE",FACE,{"disambiguationData":[OSD([subQ0])]})],"blendedInto":[makeQuery(id+"F1.opExtrude","SWEPT_FACE",FACE,{"disambiguationData":[OSD([subQ0])]})]});}
            fillet(context, id + "F3", {"entities" : qUnion([Q0, Q1, Q2, Q3, Q4, Q5, Q6, Q7, Q8, Q9, Q10, Q11, Q12, Q13, Q14, Q15]), "radius" : 2 * mm, "tangentPropagation" : true, "allowEdgeOverflow" : false});
        }
    });
